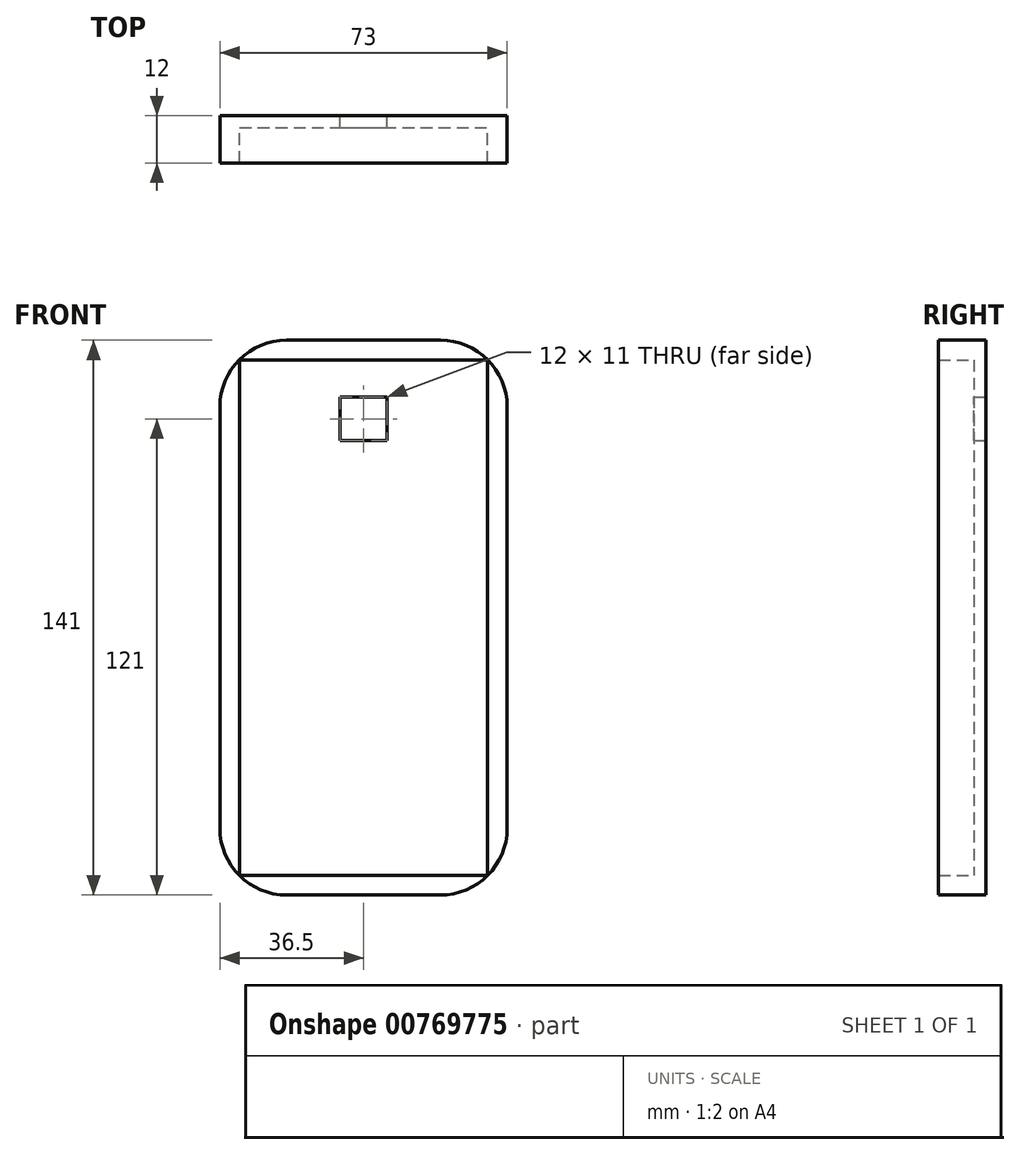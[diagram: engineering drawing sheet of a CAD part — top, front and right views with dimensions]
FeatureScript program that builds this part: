
annotation { "Feature Type Name" : "Feature", "Feature Type Description" : "" }
export const myFeature = defineFeature(function(context is Context, id is Id, definition is map)
    precondition{}
    {
        {
            var Q0;
            Q0=qCreatedBy(makeId("Front.planeOp"),FACE);
            var sketch = newSketch(context, id + "F0", { "sketchPlane" : qUnion([Q0])});
            skLineSegment(sketch, "E0.bottom", {"start": v(36.5, -70.5) * mm, "end": v(-36.5, -70.5) * mm});
            skLineSegment(sketch, "E0.top", {"start": v(36.5, 70.5) * mm, "end": v(-36.5, 70.5) * mm});
            skLineSegment(sketch, "E0.left", {"start": v(36.5, -70.5) * mm, "end": v(36.5, 70.5) * mm});
            skLineSegment(sketch, "E0.right", {"start": v(-36.5, -70.5) * mm, "end": v(-36.5, 70.5) * mm});
            skPoint(sketch, "E0.middle", {"position": v(0, 0) * mm});
            skLineSegment(sketch, "E1", {"start": v(31.5, 70.5) * mm, "end": v(31.5, -70.5) * mm});
            skLineSegment(sketch, "E2", {"start": v(-31.5, 70.5) * mm, "end": v(-31.5, -70.5) * mm});
            skLineSegment(sketch, "E3", {"start": v(31.5, -65.5) * mm, "end": v(-31.5, -65.5) * mm});
            skLineSegment(sketch, "E4", {"start": v(-31.5, 65.5) * mm, "end": v(31.5, 65.5) * mm});
            skLineSegment(sketch, "E5.bottom", {"start": v(-6, 45) * mm, "end": v(6, 45) * mm});
            skLineSegment(sketch, "E5.top", {"start": v(-6, 56) * mm, "end": v(6, 56) * mm});
            skLineSegment(sketch, "E5.left", {"start": v(-6, 45) * mm, "end": v(-6, 56) * mm});
            skLineSegment(sketch, "E5.right", {"start": v(6, 45) * mm, "end": v(6, 56) * mm});
            skPoint(sketch, "E5.middle", {"position": v(0, 50.5) * mm});
            skSolve(sketch);
        }
        {
            var Q0;
            {var subQ0=sQuery(id+"F0.wireOp",EDGE,"E3");Q0=makeQuery(id+"F0.imprint","IMPRINT",FACE,{"disambiguationData":[TD([[makeQuery(id+"F0.imprint","IMPRINT",EDGE,{"derivedFrom":subQ0}),-1.0]])]});}
            extrude(context, id + "F1", {"entities" : qUnion([Q0]), "depth" : 3 * mm, "offsetDistance" : 25 * mm});
        }
        {
            var Q0;
            Q0 = qSketchRegion(id + "F0", true);
            extrude(context, id + "F2", {"entities" : qUnion([Q0]), "operationType" : NewBodyOperationType.ADD, "depth" : 12 * mm, "offsetDistance" : 25 * mm});
        }
        {
            var Q0;
            Q0=makeQuery(id+"F2.opExtrude","SWEPT_EDGE",EDGE,{"disambiguationData":[OSD([sQuery(id+"F0.wireOp",EDGE,"E0.top"),sQuery(id+"F0.wireOp",EDGE,"E0.left")])]});
            var Q1;
            Q1=makeQuery(id+"F2.opExtrude","SWEPT_EDGE",EDGE,{"disambiguationData":[OSD([sQuery(id+"F0.wireOp",EDGE,"E0.top"),sQuery(id+"F0.wireOp",EDGE,"E0.right")])]});
            var Q2;
            Q2=makeQuery(id+"F2.opExtrude","SWEPT_EDGE",EDGE,{"disambiguationData":[OSD([sQuery(id+"F0.wireOp",EDGE,"E0.bottom"),sQuery(id+"F0.wireOp",EDGE,"E0.right")])]});
            var Q3;
            Q3=makeQuery(id+"F2.opExtrude","SWEPT_EDGE",EDGE,{"disambiguationData":[OSD([sQuery(id+"F0.wireOp",EDGE,"E0.bottom"),sQuery(id+"F0.wireOp",EDGE,"E0.left")])]});
            fillet(context, id + "F3", {"entities" : qUnion([Q0, Q1, Q2, Q3]), "radius" : 17 * mm, "tangentPropagation" : true, "allowEdgeOverflow" : false});
        }
    });
